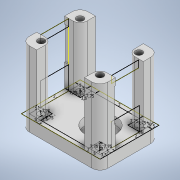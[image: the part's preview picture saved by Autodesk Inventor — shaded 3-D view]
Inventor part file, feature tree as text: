
AUTODESK INVENTOR PART (.ipt)
format: ipt  version: 2021 (Build 250183000, 183)  size: 517,632 bytes
history: native  units: mm
features: extrude x20, sketch x16, fillet x2
ambient origin geometry x8: Origin, YZ Plane, XZ Plane, XY Plane, X Axis, Y Axis, Z Axis, Center Point
bodies: Volumenkörper1 (feature_tree)
feature tree (38):
  extrude  "Extrusion1"  Depth=29.5mm
  sketch  "Skizze2"  dims[d2=6.0mm d3=0.0mm d12=3.5mm]
  sketch  "Skizze3"  dims[d13=5.0mm d14=5.0mm]
  extrude  "Extrusion2"  Depth=3.5mm
  extrude  "Extrusion3"  Depth=5.0mm
  extrude  "Extrusion4"  Depth=3.5mm
  extrude  "Extrusion5"  Depth=3.5mm
  extrude  "Extrusion6"  Depth=5.0mm
  extrude  "Extrusion7"  Depth=2.0mm
  fillet  "Rundung1"  Radius=5.0mm
  fillet  "Rundung2"  Radius=2.0mm
  sketch  "Skizze5"  dims[d17=5.0mm d18=3.5mm]
  extrude  "Extrusion8"  Depth=2.0mm
  extrude  "Extrusion9"  Depth=7.75mm
  extrude  "Extrusion10"  Depth=7.75mm
  extrude  "Extrusion11"  Depth=14.5mm
  extrude  "Extrusion14"  Depth=7.75mm
  extrude  "Extrusion15"  Depth=7.75mm
  extrude  "Extrusion16"  Depth=7.75mm
  sketch  "Skizze15"  dims[d35=7.75mm d36=7.75mm]
  sketch  "Skizze16"  dims[d37=7.75mm d38=7.75mm]
  extrude  "Extrusion17"  Depth=4.0mm TaperAngle=0.0deg
  extrude  "Extrusion18"  Depth=4.0mm TaperAngle=0.0deg
  extrude  "Extrusion19"  Depth=31.5mm TaperAngle=0.0deg
  sketch  "Skizze18"  dims[d41=31.5mm d42=0.0mm d43=4.0mm d44=0.0mm]
  extrude  "Extrusion20"  Depth=31.5mm TaperAngle=0.0deg
  extrude  "Extrusion21"  Depth=20.0mm TaperAngle=0.0deg
  extrude  "Extrusion22"  Depth=3.5mm
  sketch  "Skizze1"  dims[d0=39.5mm d1=29.5mm]
  sketch  "Skizze4"  dims[d15=3.5mm d16=5.0mm]
  sketch  "Skizze6"  dims[d19=5.0mm d20=5.0mm]
  sketch  "Skizze7"  dims[d21=3.5mm d22=5.0mm d23=5.0mm d24=2.0mm]
  sketch  "Skizze8"  dims[d25=2.0mm d28=2.0mm]
  sketch  "Skizze12"  dims[d29=2.0mm d30=7.75mm]
  sketch  "Skizze13"  dims[d31=7.75mm d32=15.4mm]
  sketch  "Skizze14"  dims[d33=14.5mm d34=14.75mm]
  sketch  "Skizze17"  dims[d39=7.75mm d40=7.75mm]
  sketch  "Skizze19"  dims[d45=10.6mm d46=4.0mm d47=0.0mm d48=31.5mm d49=0.0mm d50=31.5mm d51=0.0mm d52=20.0mm d53=0.0mm d54=3.5mm d55=4.0mm d56=16.5mm d57=3.5mm d58=7.75mm d59=7.75mm d60=3.5mm d61=20.0mm d62=0.0mm d63=20.0mm d64=0.0mm d65=14.0mm d66=16.5mm d67=7.25mm d68=3.5mm d69=20.0mm d70=0.0mm d71=14.0mm d72=16.5mm d73=7.25mm d74=3.5mm d75=20.0mm d76=0.0mm d86=4.0mm d87=0.0mm d88=4.0mm d89=0.0mm d90=10.0mm d91=0.0mm d92=10.0mm d93=0.0mm d94=10.0mm d95=0.0mm d96=0.5mm d97=0.0mm d98=0.5mm d99=0.0mm d100=0.5mm d101=0.0mm d102=0.5mm d103=0.0mm]
